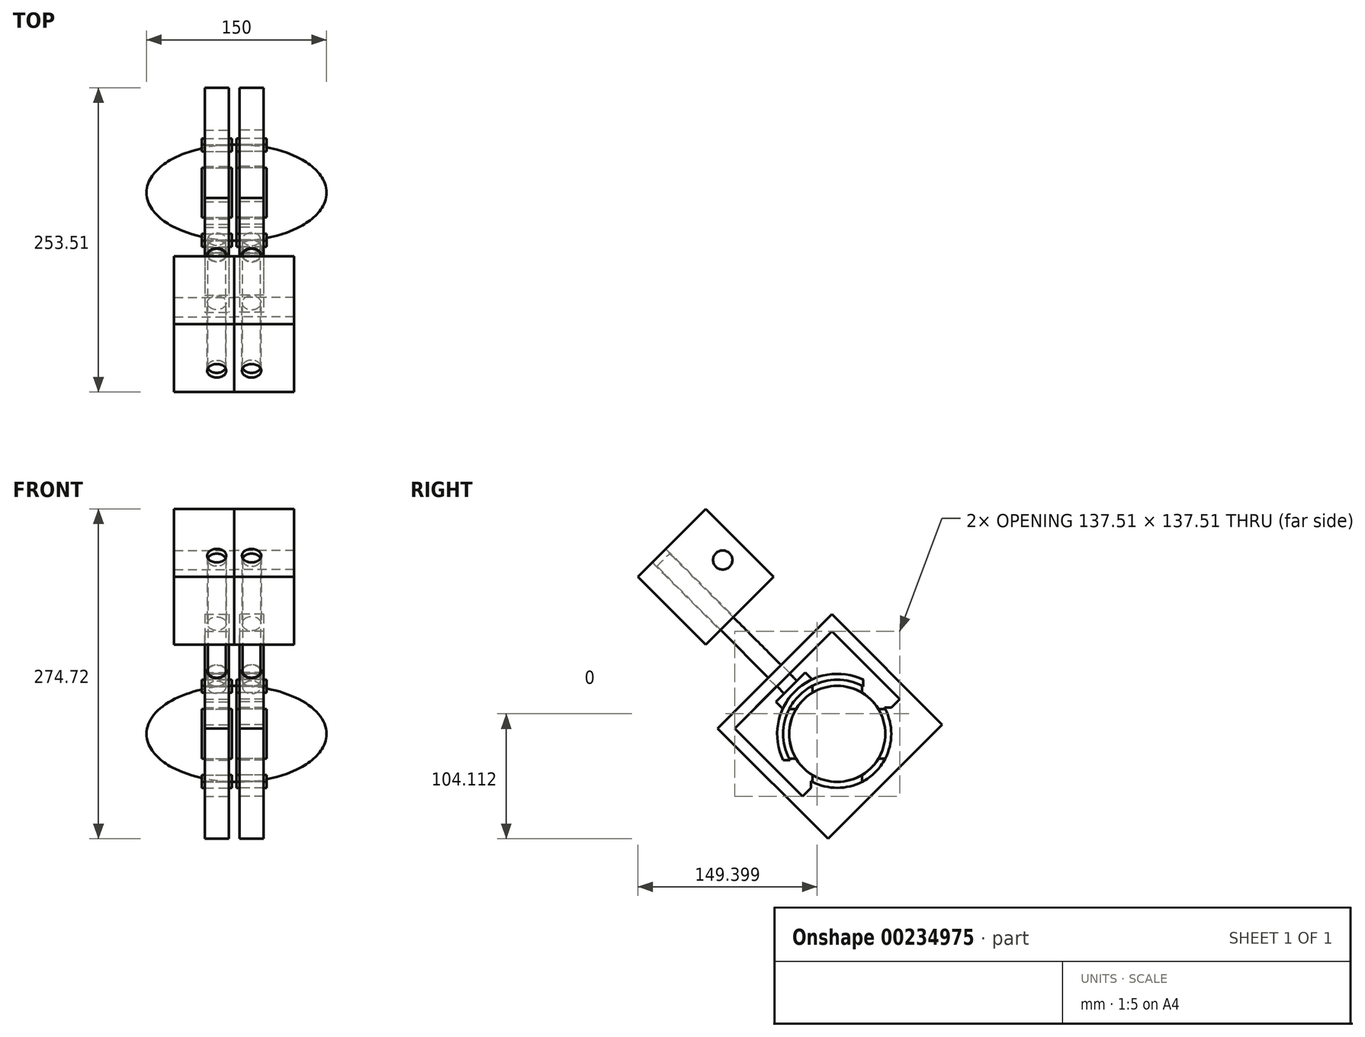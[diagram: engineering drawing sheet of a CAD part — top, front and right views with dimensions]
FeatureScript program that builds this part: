
annotation { "Feature Type Name" : "Feature", "Feature Type Description" : "" }
export const myFeature = defineFeature(function(context is Context, id is Id, definition is map)
    precondition{}
    {
        {
            var Q0;
            Q0=qCreatedBy(makeId("Front.planeOp"),FACE);
            var sketch = newSketch(context, id + "F0", { "sketchPlane" : qUnion([Q0])});
            skEllipticalArc(sketch, "E0", {});
            skLineSegment(sketch, "E1", {"start": v(0, 40) * mm, "end": v(0, 0) * mm});
            skLineSegment(sketch, "E2", {"start": v(0, 0) * mm, "end": v(-75, 0) * mm});
            skLineSegment(sketch, "E3", {"start": v(0, 0) * mm, "end": v(75, 0) * mm});
            const initialGuessF0  = {"E0": [0, 0, 1, 0, 0.075, 0.04, 0, 3.141592653589793]};
            skSetInitialGuess(sketch, initialGuessF0);
            skSolve(sketch);
        }
        {
            var Q0;
            {var subQ2=sQuery(id+"F0.wireOp",EDGE,"E1");Q0=makeQuery(id+"F0.imprint","IMPRINT",FACE,{"disambiguationData":[TD([[makeQuery(id+"F0.imprint","IMPRINT",EDGE,{"derivedFrom":subQ2}),-1.0]])]});}
            var Q1;
            Q1=sQuery(id+"F0.wireOp",EDGE,"E2");
            revolve(context, id + "F1", {"entities" : qUnion([Q0]), "axis" : qUnion([Q1]), "revolveType" : RevolveType.FULL});
        }
        {
            var Q0;
            {var subQ2=sQuery(id+"F0.wireOp",EDGE,"E1");Q0=makeQuery(id+"F0.imprint","IMPRINT",FACE,{"disambiguationData":[TD([[makeQuery(id+"F0.imprint","IMPRINT",EDGE,{"derivedFrom":subQ2}),1.0]])]});}
            var Q1;
            Q1=sQuery(id+"F0.wireOp",EDGE,"E3");
            revolve(context, id + "F2", {"entities" : qUnion([Q0]), "axis" : qUnion([Q1]), "revolveType" : RevolveType.FULL});
        }
        {
            var Q0;
            Q0=qCreatedBy(makeId("Right.planeOp"),FACE);
            var sketch = newSketch(context, id + "F3", { "sketchPlane" : qUnion([Q0])});
            skArc(sketch, "E4", {"start": v(-20.62, -34.28) * mm, "mid": v(0, -40) * mm, "end": v(20.62, -34.28) * mm});
            skArc(sketch, "E5", {"start": v(-40, 20.62) * mm, "mid": v(-45, 0) * mm, "end": v(-40, -20.62) * mm});
            skLineSegment(sketch, "E6", {"start": v(0, 0) * mm, "end": v(-45, 0) * mm});
            skLineSegment(sketch, "E7", {"start": v(0, 0) * mm, "end": v(0, 45) * mm});
            skLineSegment(sketch, "E8", {"start": v(0, 0) * mm, "end": v(45, 0) * mm});
            skLineSegment(sketch, "E9", {"start": v(0, 0) * mm, "end": v(0, -45) * mm});
            skLineSegment(sketch, "E10", {"start": v(-40, -20.62) * mm, "end": v(-34.28, -20.62) * mm});
            skLineSegment(sketch, "E11", {"start": v(-40, 20.62) * mm, "end": v(-34.28, 20.62) * mm});
            skLineSegment(sketch, "E12", {"start": v(20.62, 40) * mm, "end": v(20.62, 34.28) * mm});
            skLineSegment(sketch, "E13", {"start": v(-20.62, 40) * mm, "end": v(-20.62, 34.28) * mm});
            skLineSegment(sketch, "E14", {"start": v(40, 20.62) * mm, "end": v(34.28, 20.62) * mm});
            skPoint(sketch, "E14.startSnap0", {"position": v(-33.24, 20.62) * mm});
            skLineSegment(sketch, "E15", {"start": v(40, -20.62) * mm, "end": v(34.28, -20.62) * mm});
            skLineSegment(sketch, "E16", {"start": v(20.62, -40) * mm, "end": v(20.62, -34.28) * mm});
            skLineSegment(sketch, "E17", {"start": v(-20.62, -40) * mm, "end": v(-20.62, -34.28) * mm});
            skPoint(sketch, "E18.orphan", {"position": v(-26.47, 20.62) * mm});
            skArc(sketch, "E19.trimOffspring", {"start": v(20.62, 40) * mm, "mid": v(0, 45) * mm, "end": v(-20.62, 40) * mm});
            skPoint(sketch, "E20.start.orphan", {"position": v(40, 0) * mm});
            skArc(sketch, "E21.trimOffspring", {"start": v(40, -20.62) * mm, "mid": v(45, 0) * mm, "end": v(40, 20.62) * mm});
            skArc(sketch, "E22.trimOffspring", {"start": v(-20.62, -40) * mm, "mid": v(0, -45) * mm, "end": v(20.62, -40) * mm});
            skArc(sketch, "E23.trimOffspring", {"start": v(34.28, -20.62) * mm, "mid": v(40, 0) * mm, "end": v(34.28, 20.62) * mm});
            skArc(sketch, "E24.trimOffspring", {"start": v(20.62, 34.28) * mm, "mid": v(0, 40) * mm, "end": v(-20.62, 34.28) * mm});
            skArc(sketch, "E25.trimOffspring", {"start": v(-34.28, 20.62) * mm, "mid": v(-40, 0) * mm, "end": v(-34.28, -20.62) * mm});
            skSolve(sketch);
        }
        {
            var Q0;
            Q0 = qSketchRegion(id + "F3", true);
            extrude(context, id + "F4", {"entities" : qUnion([Q0]), "depth" : 25 * mm});
        }
        {
            var Q0;
            Q0=qCreatedBy(makeId("Right.planeOp"),FACE);
            cPlane(context, id + "F5", {"entities" : qUnion([Q0]), "cplaneType" : CPlaneType.OFFSET, "offset" : 12.5 * mm, "width" : 150 * mm, "height" : 150 * mm});
        }
        {
            var Q0;
            Q0=qCreatedBy(id+"F5.planeOp",FACE);
            var sketch = newSketch(context, id + "F6", { "sketchPlane" : qUnion([Q0])});
            skArc(sketch, "E26", {"start": v(-21.8, -39.37) * mm, "mid": v(31.82, -31.82) * mm, "end": v(39.37, 21.8) * mm});
            skLineSegment(sketch, "E27", {"start": v(-45, -21.8) * mm, "end": v(-39.37, -21.8) * mm});
            skLineSegment(sketch, "E28", {"start": v(21.8, 45) * mm, "end": v(21.8, 39.37) * mm});
            skLineSegment(sketch, "E29", {"start": v(45, 21.8) * mm, "end": v(39.37, 21.8) * mm});
            skLineSegment(sketch, "E30", {"start": v(-21.8, -45) * mm, "end": v(-21.8, -39.37) * mm});
            skArc(sketch, "E31.trimOffspring", {"start": v(21.8, 45) * mm, "mid": v(-35.36, 35.36) * mm, "end": v(-45, -21.8) * mm});
            skPoint(sketch, "E32.start.orphan", {"position": v(0, 45) * mm});
            skArc(sketch, "E33.trimOffspring", {"start": v(21.8, 39.37) * mm, "mid": v(-31.82, 31.82) * mm, "end": v(-39.37, -21.8) * mm});
            skPoint(sketch, "E34.orphan", {"position": v(45, 0) * mm});
            skPoint(sketch, "E35.orphan", {"position": v(0, -45) * mm});
            skLineSegment(sketch, "E36", {"start": v(45, 21.8) * mm, "end": v(59.14, 35.94) * mm});
            skLineSegment(sketch, "E37", {"start": v(59.14, 35.94) * mm, "end": v(87.43, 7.65) * mm});
            skLineSegment(sketch, "E38", {"start": v(87.43, 7.65) * mm, "end": v(-7.65, -87.43) * mm});
            skLineSegment(sketch, "E39", {"start": v(-7.65, -87.43) * mm, "end": v(-35.94, -59.14) * mm});
            skLineSegment(sketch, "E40", {"start": v(-35.94, -59.14) * mm, "end": v(-21.8, -45) * mm});
            skLineSegment(sketch, "E41", {"start": v(0, 0) * mm, "end": v(59.01, 0) * mm});
            skLineSegment(sketch, "E42", {"start": v(59.14, 35.94) * mm, "end": v(-4.5, 99.58) * mm});
            skLineSegment(sketch, "E43", {"start": v(-35.94, -59.14) * mm, "end": v(-99.58, 4.5) * mm});
            skLineSegment(sketch, "E44", {"start": v(52.07, 28.87) * mm, "end": v(-4.5, 85.43) * mm});
            skLineSegment(sketch, "E45", {"start": v(-28.87, -52.07) * mm, "end": v(-85.43, 4.5) * mm});
            skLineSegment(sketch, "E46", {"start": v(-4.5, 85.43) * mm, "end": v(-85.43, 4.5) * mm});
            skLineSegment(sketch, "E47", {"start": v(-4.5, 99.58) * mm, "end": v(-99.58, 4.5) * mm});
            skSolve(sketch);
        }
        {
            var Q0;
            Q0 = qSketchRegion(id + "F6", true);
            extrude(context, id + "F7", {"entities" : qUnion([Q0]), "endBound" : BoundingType.SYMMETRIC, "depth" : 20 * mm});
        }
        {
            var Q0;
            Q0=qCreatedBy(id+"F5.planeOp",FACE);
            var sketch = newSketch(context, id + "F8", { "sketchPlane" : qUnion([Q0])});
            skArc(sketch, "E48", {"start": v(21.63, 39.46) * mm, "mid": v(-31.89, 31.75) * mm, "end": v(-39.37, -21.8) * mm});
            skArc(sketch, "E49", {"start": v(21.8, 45) * mm, "mid": v(-35.36, 35.36) * mm, "end": v(-45, -21.8) * mm});
            skLineSegment(sketch, "E50", {"start": v(21.63, 45) * mm, "end": v(21.8, 45) * mm});
            skLineSegment(sketch, "E51", {"start": v(-45, 21.8) * mm, "end": v(-39.37, 21.8) * mm});
            skLineSegment(sketch, "E52", {"start": v(-45, -21.8) * mm, "end": v(-39.37, -21.8) * mm});
            skLineSegment(sketch, "E53", {"start": v(-21.8, 45) * mm, "end": v(-21.8, 39.37) * mm});
            skLineSegment(sketch, "E54", {"start": v(21.63, 45) * mm, "end": v(21.63, 39.46) * mm});
            skPoint(sketch, "E55.orphan", {"position": v(43.26, 45) * mm});
            skPoint(sketch, "E56.orphan", {"position": v(0, 45) * mm});
            skPoint(sketch, "E57.orphan", {"position": v(-45, 0) * mm});
            skSolve(sketch);
        }
        {
            var Q0;
            Q0 = qSketchRegion(id + "F8", true);
            extrude(context, id + "F9", {"entities" : qUnion([Q0]), "endBound" : BoundingType.SYMMETRIC, "depth" : 20 * mm});
        }
        {
            var Q0;
            Q0=qCreatedBy(id+"F5.planeOp",FACE);
            var sketch = newSketch(context, id + "F10", { "sketchPlane" : qUnion([Q0])});
            skArc(sketch, "E58", {"start": v(-20.83, 45.45) * mm, "mid": v(-35.36, 35.36) * mm, "end": v(-45.45, 20.83) * mm});
            skLineSegment(sketch, "E59", {"start": v(-45.45, 20.83) * mm, "end": v(-51.02, 26.57) * mm});
            skLineSegment(sketch, "E60", {"start": v(-20.83, 45.45) * mm, "end": v(-26.49, 51.11) * mm});
            skPoint(sketch, "E61.orphan", {"position": v(-27.5, 27.5) * mm});
            skPoint(sketch, "E62.orphan", {"position": v(0, 55) * mm});
            skPoint(sketch, "E63.orphan", {"position": v(-55, 0) * mm});
            skLineSegment(sketch, "E64", {"start": v(-26.49, 51.11) * mm, "end": v(-51.02, 26.57) * mm});
            skSolve(sketch);
        }
        {
            var Q0;
            Q0 = qSketchRegion(id + "F10", true);
            extrude(context, id + "F11", {"entities" : qUnion([Q0]), "endBound" : BoundingType.SYMMETRIC, "depth" : 20 * mm});
        }
        {
            var Q0;
            Q0=makeQuery(id+"F11.opExtrude","SWEPT_FACE",FACE,{"disambiguationData":[OSD([sQuery(id+"F10.wireOp",EDGE,"E64")])]});
            var sketch = newSketch(context, id + "F12", { "sketchPlane" : qUnion([Q0])});
            skLineSegment(sketch, "E65", {"start": v(12.5, 17.41) * mm, "end": v(12.5, -17.29) * mm});
            skCircle(sketch, "E66", {"center": v(12.5, 0) * mm, "radius": 7.5 * mm});
            skSolve(sketch);
        }
        {
            var Q0;
            Q0 = qSketchRegion(id + "F12", true);
            extrude(context, id + "F13", {"entities" : qUnion([Q0]), "depth" : 150 * mm});
        }
        {
            var Q0;
            Q0=makeQuery(id+"F7.opExtrude","SWEPT_FACE",FACE,{"disambiguationData":[OSD([sQuery(id+"F6.wireOp",EDGE,"E47")])]});
            var sketch = newSketch(context, id + "F14", { "sketchPlane" : qUnion([Q0])});
            skLineSegment(sketch, "E67", {"start": v(12.5, 67.23) * mm, "end": v(12.5, -67.23) * mm});
            skCircle(sketch, "E68", {"center": v(12.5, 0) * mm, "radius": 8 * mm});
            skSolve(sketch);
        }
        {
            var Q0;
            Q0 = qSketchRegion(id + "F14", true);
            extrude(context, id + "F15", {"entities" : qUnion([Q0]), "operationType" : NewBodyOperationType.REMOVE, "oppositeDirection" : true, "depth" : 10 * mm});
        }
        {
            var Q0;
            Q0=makeQuery(id+"F13.opExtrude","CAP_FACE",FACE,{"disambiguationData":[OSD([sQuery(id+"F12.wireOp",EDGE,"E66")])],"isStart":false});
            cPlane(context, id + "F16", {"entities" : qUnion([Q0]), "cplaneType" : CPlaneType.OFFSET, "offset" : 75 * mm, "oppositeDirection" : true, "width" : 150 * mm, "height" : 150 * mm});
        }
        {
            var Q0;
            Q0=qCreatedBy(id+"F16.planeOp",FACE);
            var sketch = newSketch(context, id + "F17", { "sketchPlane" : qUnion([Q0])});
            skLineSegment(sketch, "E69", {"start": v(0, 0) * mm, "end": v(25, 0) * mm});
            skLineSegment(sketch, "E70.bottom", {"start": v(27, 25) * mm, "end": v(-2, 25) * mm});
            skLineSegment(sketch, "E70.top", {"start": v(27, -25) * mm, "end": v(-2, -25) * mm});
            skLineSegment(sketch, "E70.left", {"start": v(27, 25) * mm, "end": v(27, -25) * mm});
            skLineSegment(sketch, "E70.right", {"start": v(-2, 25) * mm, "end": v(-2, -25) * mm});
            skPoint(sketch, "E70.middle", {"position": v(12.5, 0) * mm});
            skCircle(sketch, "E71", {"center": v(12.5, 0) * mm, "radius": 8 * mm});
            skLineSegment(sketch, "E72", {"start": v(-2, 25) * mm, "end": v(-2, 55) * mm});
            skLineSegment(sketch, "E73", {"start": v(-2, 55) * mm, "end": v(27, 55) * mm});
            skLineSegment(sketch, "E74", {"start": v(27, 55) * mm, "end": v(27, 25) * mm});
            skLineSegment(sketch, "E75", {"start": v(27, -25) * mm, "end": v(48, -25) * mm});
            skLineSegment(sketch, "E76", {"start": v(48, -25) * mm, "end": v(48, 55) * mm});
            skLineSegment(sketch, "E77", {"start": v(48, 55) * mm, "end": v(27, 55) * mm});
            skSolve(sketch);
        }
        {
            var Q0;
            Q0 = qSketchRegion(id + "F17", true);
            extrude(context, id + "F18", {"entities" : qUnion([Q0]), "depth" : 80 * mm});
        }
        {
            var Q0;
            Q0=makeQuery(id+"F18.opExtrude","SWEPT_FACE",FACE,{"disambiguationData":[OSD([sQuery(id+"F17.wireOp",EDGE,"E70.right"),sQuery(id+"F17.wireOp",EDGE,"E72")])]});
            var sketch = newSketch(context, id + "F19", { "sketchPlane" : qUnion([Q0])});
            skLineSegment(sketch, "E78", {"start": v(81.23, 159) * mm, "end": v(109.51, 130.72) * mm});
            skLineSegment(sketch, "E79", {"start": v(81.23, 102.44) * mm, "end": v(137.8, 159) * mm});
            skPoint(sketch, "E80.orphan", {"position": v(137.8, 102.43) * mm});
            skCircle(sketch, "E81", {"center": v(95.37, 144.86) * mm, "radius": 8 * mm});
            skSolve(sketch);
        }
        {
            var Q0;
            Q0 = qSketchRegion(id + "F19", true);
            extrude(context, id + "F20", {"entities" : qUnion([Q0]), "operationType" : NewBodyOperationType.REMOVE, "oppositeDirection" : true, "depth" : 50 * mm});
        }
        {
            var Q0;
            Q0=makeQuery(id+"F18.opExtrude","CAP_FACE",FACE,{"disambiguationData":[OSD([sQuery(id+"F17.wireOp",EDGE,"E70.top"),sQuery(id+"F17.wireOp",EDGE,"E70.right"),sQuery(id+"F17.wireOp",EDGE,"E71"),sQuery(id+"F17.wireOp",EDGE,"E72"),sQuery(id+"F17.wireOp",EDGE,"E73"),sQuery(id+"F17.wireOp",EDGE,"E75"),sQuery(id+"F17.wireOp",EDGE,"E76"),sQuery(id+"F17.wireOp",EDGE,"E77")])],"isStart":true});
            var sketch = newSketch(context, id + "F21", { "sketchPlane" : qUnion([Q0])});
            skLineSegment(sketch, "E82", {"start": v(2, -25) * mm, "end": v(2, 55) * mm});
            skLineSegment(sketch, "E83", {"start": v(2, 55) * mm, "end": v(52, 55) * mm});
            skLineSegment(sketch, "E84", {"start": v(52, 55) * mm, "end": v(52, -25) * mm});
            skLineSegment(sketch, "E85", {"start": v(52, -25) * mm, "end": v(2, -25) * mm});
            skLineSegment(sketch, "E86", {"start": v(52, -25) * mm, "end": v(52, 25) * mm});
            skLineSegment(sketch, "E87", {"start": v(52, 25) * mm, "end": v(31, 25) * mm});
            skLineSegment(sketch, "E88", {"start": v(31, 25) * mm, "end": v(2, 25) * mm});
            skLineSegment(sketch, "E89", {"start": v(16.5, 25) * mm, "end": v(16.5, 0) * mm});
            skCircle(sketch, "E90", {"center": v(16.5, 0) * mm, "radius": 8 * mm});
            skSolve(sketch);
        }
        {
            var Q0;
            Q0 = qSketchRegion(id + "F21", true);
            extrude(context, id + "F22", {"entities" : qUnion([Q0]), "oppositeDirection" : true, "depth" : 80 * mm});
        }
        {
            var Q0;
            Q0=makeQuery(id+"F22.opExtrude","SWEPT_FACE",FACE,{"disambiguationData":[OSD([sQuery(id+"F21.wireOp",EDGE,"E82")])]});
            var sketch = newSketch(context, id + "F23", { "sketchPlane" : qUnion([Q0])});
            skLineSegment(sketch, "E91", {"start": v(-52.94, 130.72) * mm, "end": v(-67.09, 116.58) * mm});
            skLineSegment(sketch, "E92", {"start": v(-67.09, 116.58) * mm, "end": v(-95.37, 144.86) * mm});
            skCircle(sketch, "E93", {"center": v(-95.37, 144.86) * mm, "radius": 8 * mm});
            skSolve(sketch);
        }
        {
            var Q0;
            Q0 = qSketchRegion(id + "F23", true);
            extrude(context, id + "F24", {"entities" : qUnion([Q0]), "operationType" : NewBodyOperationType.REMOVE, "oppositeDirection" : true, "depth" : 50 * mm});
        }
        {
            var Q0;
            Q0=makeQuery(id+"F13.opExtrude","SWEPT_BODY",BODY,{"disambiguationData":[OSD([sQuery(id+"F12.wireOp",EDGE,"E66")])]});
            var Q1;
            Q1=makeQuery(id+"F7.opExtrude","SWEPT_BODY",BODY,{"disambiguationData":[OSD([sQuery(id+"F6.wireOp",EDGE,"E26"),sQuery(id+"F6.wireOp",EDGE,"E29"),sQuery(id+"F6.wireOp",EDGE,"E30"),sQuery(id+"F6.wireOp",EDGE,"E36"),sQuery(id+"F6.wireOp",EDGE,"E37"),sQuery(id+"F6.wireOp",EDGE,"E38"),sQuery(id+"F6.wireOp",EDGE,"E39"),sQuery(id+"F6.wireOp",EDGE,"E40"),sQuery(id+"F6.wireOp",EDGE,"E42"),sQuery(id+"F6.wireOp",EDGE,"E43"),sQuery(id+"F6.wireOp",EDGE,"E44"),sQuery(id+"F6.wireOp",EDGE,"E45"),sQuery(id+"F6.wireOp",EDGE,"E46"),sQuery(id+"F6.wireOp",EDGE,"E47")])]});
            var Q2;
            Q2=makeQuery(id+"F11.opExtrude","SWEPT_BODY",BODY,{"disambiguationData":[OSD([sQuery(id+"F10.wireOp",EDGE,"E58"),sQuery(id+"F10.wireOp",EDGE,"E59"),sQuery(id+"F10.wireOp",EDGE,"E60"),sQuery(id+"F10.wireOp",EDGE,"E64")])]});
            var Q3;
            Q3=makeQuery(id+"F4.opExtrude","SWEPT_BODY",BODY,{"disambiguationData":[OSD([sQuery(id+"F3.wireOp",EDGE,"E12"),sQuery(id+"F3.wireOp",EDGE,"E13"),sQuery(id+"F3.wireOp",EDGE,"E19.trimOffspring"),sQuery(id+"F3.wireOp",EDGE,"E24.trimOffspring")])]});
            var Q4;
            Q4=makeQuery(id+"F9.opExtrude","SWEPT_BODY",BODY,{"disambiguationData":[OSD([sQuery(id+"F8.wireOp",EDGE,"E48"),sQuery(id+"F8.wireOp",EDGE,"E49"),sQuery(id+"F8.wireOp",EDGE,"E50"),sQuery(id+"F8.wireOp",EDGE,"E52"),sQuery(id+"F8.wireOp",EDGE,"E54")])]});
            var Q5;
            Q5=makeQuery(id+"F4.opExtrude","SWEPT_BODY",BODY,{"disambiguationData":[OSD([sQuery(id+"F3.wireOp",EDGE,"E14"),sQuery(id+"F3.wireOp",EDGE,"E15"),sQuery(id+"F3.wireOp",EDGE,"E21.trimOffspring"),sQuery(id+"F3.wireOp",EDGE,"E23.trimOffspring")])]});
            var Q6;
            Q6=makeQuery(id+"F4.opExtrude","SWEPT_BODY",BODY,{"disambiguationData":[OSD([sQuery(id+"F3.wireOp",EDGE,"E4"),sQuery(id+"F3.wireOp",EDGE,"E16"),sQuery(id+"F3.wireOp",EDGE,"E17"),sQuery(id+"F3.wireOp",EDGE,"E22.trimOffspring")])]});
            var Q7;
            Q7=makeQuery(id+"F4.opExtrude","SWEPT_BODY",BODY,{"disambiguationData":[OSD([sQuery(id+"F3.wireOp",EDGE,"E5"),sQuery(id+"F3.wireOp",EDGE,"E10"),sQuery(id+"F3.wireOp",EDGE,"E11"),sQuery(id+"F3.wireOp",EDGE,"E25.trimOffspring")])]});
            var Q8;
            Q8=makeQuery(id+"F18.opExtrude","SWEPT_FACE",FACE,{"disambiguationData":[OSD([sQuery(id+"F17.wireOp",EDGE,"E70.right"),sQuery(id+"F17.wireOp",EDGE,"E72")])]});
            mirror(context, id + "F25", {"entities" : qUnion([Q0, Q1, Q2, Q3, Q4, Q5, Q6, Q7]), "mirrorPlane" : qUnion([Q8])});
        }
    });
